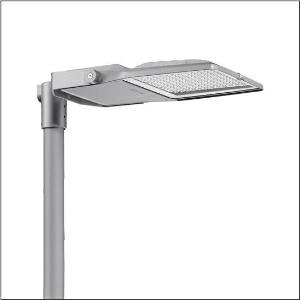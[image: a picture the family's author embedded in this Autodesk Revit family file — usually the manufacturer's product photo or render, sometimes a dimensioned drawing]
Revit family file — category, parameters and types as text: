
# Revit family: floodlight_fl_21_iq_midi___pl64_5xa7781e4e3a_69c6
name_source: partatom
category: Lighting Fixtures
units: mm (PartAtom-declared; Revit-internal decimal feet)

## family parameters
Cut with Voids When Loaded = No
Host = Face
Light Source = No
Part Type = Normal
Room Calculation Point = No
Round Connector Dimension = Use Diameter
Shared = No

## types (1)
- --- (1 x LED, 27050 lm, 208.1 W, 4000K)
    Apparent Load = 208 VA
    CIE Flux Codes = 28 80 98 100 100
    Color Rendering = 70
    Color Temperature = 4000K
    Default Elevation = 1800 mm
    Description = Floodlight FL 21 iQ midi, floodlight, primary light control with lens, of PMMA, primary optical cover: protective disc, of toughened safety glass, transparent, light distribution: PL64, light emission: direct distribution, installation type: surface-mounted, LED, High Power LED, rated luminous flux: 27.050lm, luminous efficacy: 130lm/W, light colour: 740, colour temperature: 4000K, control gear: ECG iQ, control: optimised constant luminous flux control (CLO 2.0), Desk-Remote (wireless, voltage-free reading and setting of iQ features in the workshop via application-optimized NFC function/RFID function), Light-Fading, Smart-Wire, Night-Set, Lumen-Switch, Temp-Guard, Auto-Match, with terminal, 6-pole, mains connection: 220..240V, AC, 50/60Hz, start of lifetime: 208W, end of service life: 227W, reduction: 90W, luminaire housing, of diecast aluminium, powder-coated, Siteco® metallic grey (DB 702S), corrosivity category C5 mid according to DIN EN ISO 12944, sealing non-destructively replaceable, please order mast flange separately, mast bracket, of steel, galvanised, powder-coated, Siteco® metallic grey (DB 702S), protection rating (complete): IP66, insulation class (complete): insulation class II (safety insulation), certification: CE, protection symbol: D, impact resistance: IK08, permissible operating ambient temperature: -40..+40°C, permissible operating ambient temperature for outdoor applications: -40..+50°C, standard: DIN EN 12944, LABS conformity tested according to VDMA 24364:2018-05, packaging unit: 1 piece

Light Distribution: PL64
    Height = 76 mm
    Lamp = 1 x LED
    Lamp Light Flux = 27050 lm
    Lamp Power = 208.1 W
    Lamp count = 1
    Length = 657 mm
    Luminous efficacy = 130 lm/W
    Manufacturer = Siteco
    ModVariant = No
    Model = 5XA7781E4E3A
    Number of Poles = 1
    OnlyDefault = Yes
    Power Factor = 1
    Product Name = Floodlight FL 21 iQ midi | PL64
    Product group = floodlight | pylon annexe
    ProductGroupID = 6200
    Protection Class = Protection class II
    Protection Degree = IP 66
    RLX_Detail_Level = 1
    RLX_Emergency_Light_Flux = 0 lm
    RLX_Emergency_Type = 0
    RLX_Emergency_Type_DB = No
    RlxData = <blob elided: 153585 chars, md5=2644ed89>
    Socket = socket
    Standby Power = 0 W
    System Light Flux = 27050 lm
    System Power = 208 W
    Type Comments = factory setting: luminous flux: 100 % | dim-lin: 254 | 710 mA
    Type Image = l_1007123.jpg
    URL = http://relux.com
    VarID = @adj_037337
    Voltage = 0 V
    Weight = 0.00 kg
    Width = 442 mm

## geometry (parser evidence)
native form markers: Blend x4, Sweep x14
no freeform markers — native parametric forms only
